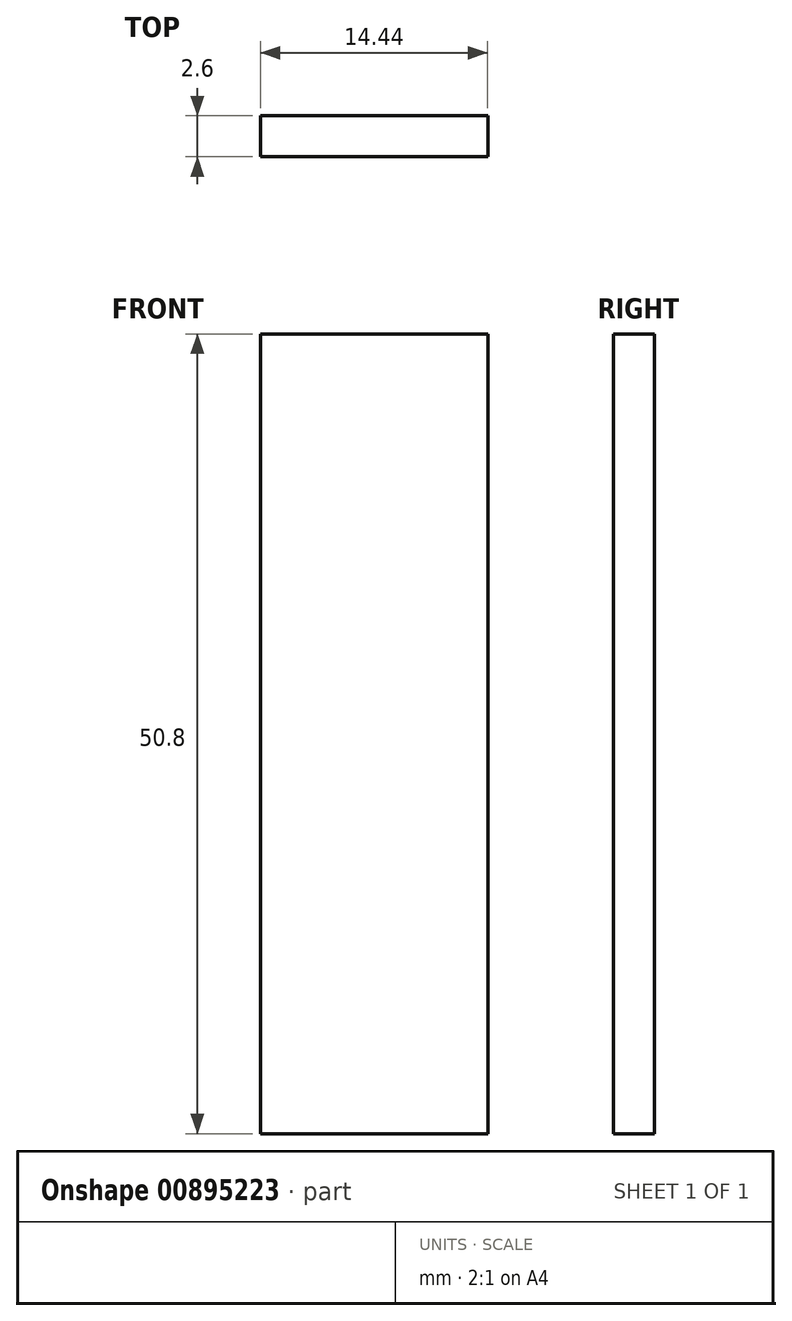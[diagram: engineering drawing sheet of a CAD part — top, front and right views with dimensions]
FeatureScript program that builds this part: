
annotation { "Feature Type Name" : "Feature", "Feature Type Description" : "" }
export const myFeature = defineFeature(function(context is Context, id is Id, definition is map)
    precondition{}
    {
        {
            var Q0;
            Q0=qCreatedBy(makeId("Top.planeOp"),FACE);
            var sketch = newSketch(context, id + "F0", { "sketchPlane" : qUnion([Q0])});
            skLineSegment(sketch, "E0.bottom", {"start": v(7.22, 1.3) * mm, "end": v(-7.22, 1.3) * mm});
            skLineSegment(sketch, "E0.top", {"start": v(7.22, -1.3) * mm, "end": v(-7.22, -1.3) * mm});
            skLineSegment(sketch, "E0.left", {"start": v(7.22, 1.3) * mm, "end": v(7.22, -1.3) * mm});
            skLineSegment(sketch, "E0.right", {"start": v(-7.22, 1.3) * mm, "end": v(-7.22, -1.3) * mm});
            skPoint(sketch, "E0.middle", {"position": v(0, 0) * mm});
            skSolve(sketch);
        }
        {
            var Q0;
            Q0 = qSketchRegion(id + "F0", true);
            extrude(context, id + "F1", {"entities" : qUnion([Q0]), "endBound" : BoundingType.SYMMETRIC, "depth" : 50.8 * mm, "offsetDistance" : 25.4 * mm});
        }
    });
